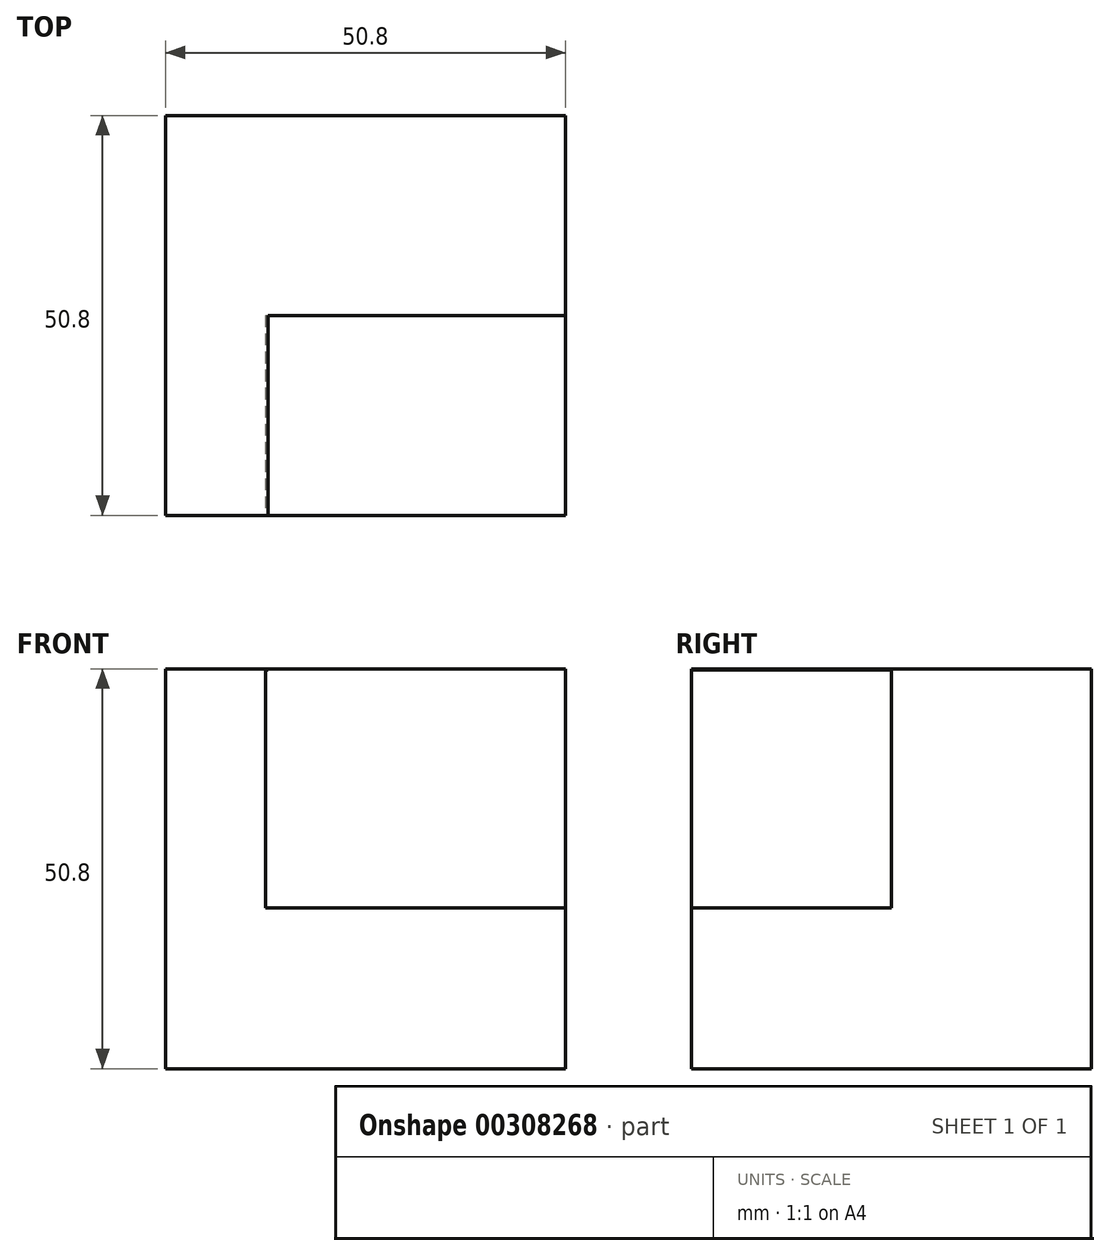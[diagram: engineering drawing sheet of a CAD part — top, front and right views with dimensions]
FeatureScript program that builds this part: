
annotation { "Feature Type Name" : "Feature", "Feature Type Description" : "" }
export const myFeature = defineFeature(function(context is Context, id is Id, definition is map)
    precondition{}
    {
        {
            var Q0;
            Q0=qCreatedBy(makeId("Front.planeOp"),FACE);
            var sketch = newSketch(context, id + "F0", { "sketchPlane" : qUnion([Q0])});
            skLineSegment(sketch, "E0", {"start": v(-55.78, -33.97) * mm, "end": v(-4.98, -33.97) * mm});
            skLineSegment(sketch, "E1", {"start": v(-4.98, -33.97) * mm, "end": v(-4.98, 16.83) * mm});
            skLineSegment(sketch, "E2", {"start": v(-4.98, 16.83) * mm, "end": v(-55.78, 16.83) * mm});
            skLineSegment(sketch, "E3", {"start": v(-55.78, 16.83) * mm, "end": v(-55.78, -33.97) * mm});
            skSolve(sketch);
        }
        {
            var Q0;
            Q0 = qSketchRegion(id + "F0", true);
            extrude(context, id + "F1", {"entities" : qUnion([Q0]), "oppositeDirection" : true, "depth" : 50.8 * mm});
        }
        {
            var Q0;
            Q0=qCreatedBy(makeId("Front.planeOp"),FACE);
            var sketch = newSketch(context, id + "F2", { "sketchPlane" : qUnion([Q0])});
            skLineSegment(sketch, "E4", {"start": v(-4.85, -13.55) * mm, "end": v(-43.07, -13.55) * mm});
            skLineSegment(sketch, "E5", {"start": v(-43.07, -13.55) * mm, "end": v(-43.07, 16.69) * mm});
            skLineSegment(sketch, "E6", {"start": v(-43.07, 16.69) * mm, "end": v(-5.13, 16.69) * mm});
            skLineSegment(sketch, "E7", {"start": v(-5.13, 16.69) * mm, "end": v(-4.85, -13.55) * mm});
            skSolve(sketch);
        }
        {
            var Q0;
            Q0=makeQuery(id+"F2.imprint","IMPRINT",FACE,{"disambiguationData":[TD([[makeQuery(id+"F2.imprint","IMPRINT",EDGE,{"derivedFrom":sQuery(id+"F2.wireOp",EDGE,"E4")}),-1.0]])]});
            extrude(context, id + "F3", {"entities" : qUnion([Q0]), "operationType" : NewBodyOperationType.REMOVE, "oppositeDirection" : true, "depth" : 25.4 * mm});
        }
        {
            var Q0;
            Q0=qCreatedBy(makeId("Front.planeOp"),FACE);
            var sketch = newSketch(context, id + "F4", { "sketchPlane" : qUnion([Q0])});
            skLineSegment(sketch, "E8", {"start": v(-42.79, 16.97) * mm, "end": v(-4.56, 16.97) * mm});
            skLineSegment(sketch, "E9", {"start": v(-4.56, 16.97) * mm, "end": v(-4.56, -12.12) * mm});
            skLineSegment(sketch, "E10", {"start": v(-4.56, -12.12) * mm, "end": v(-41.93, -12.12) * mm});
            skLineSegment(sketch, "E11", {"start": v(-41.93, -12.12) * mm, "end": v(-42.79, 16.97) * mm});
            skSolve(sketch);
        }
        {
            var Q0;
            Q0 = qSketchRegion(id + "F4", true);
            extrude(context, id + "F5", {"entities" : qUnion([Q0]), "operationType" : NewBodyOperationType.REMOVE, "oppositeDirection" : true, "depth" : 25.4 * mm});
        }
    });
